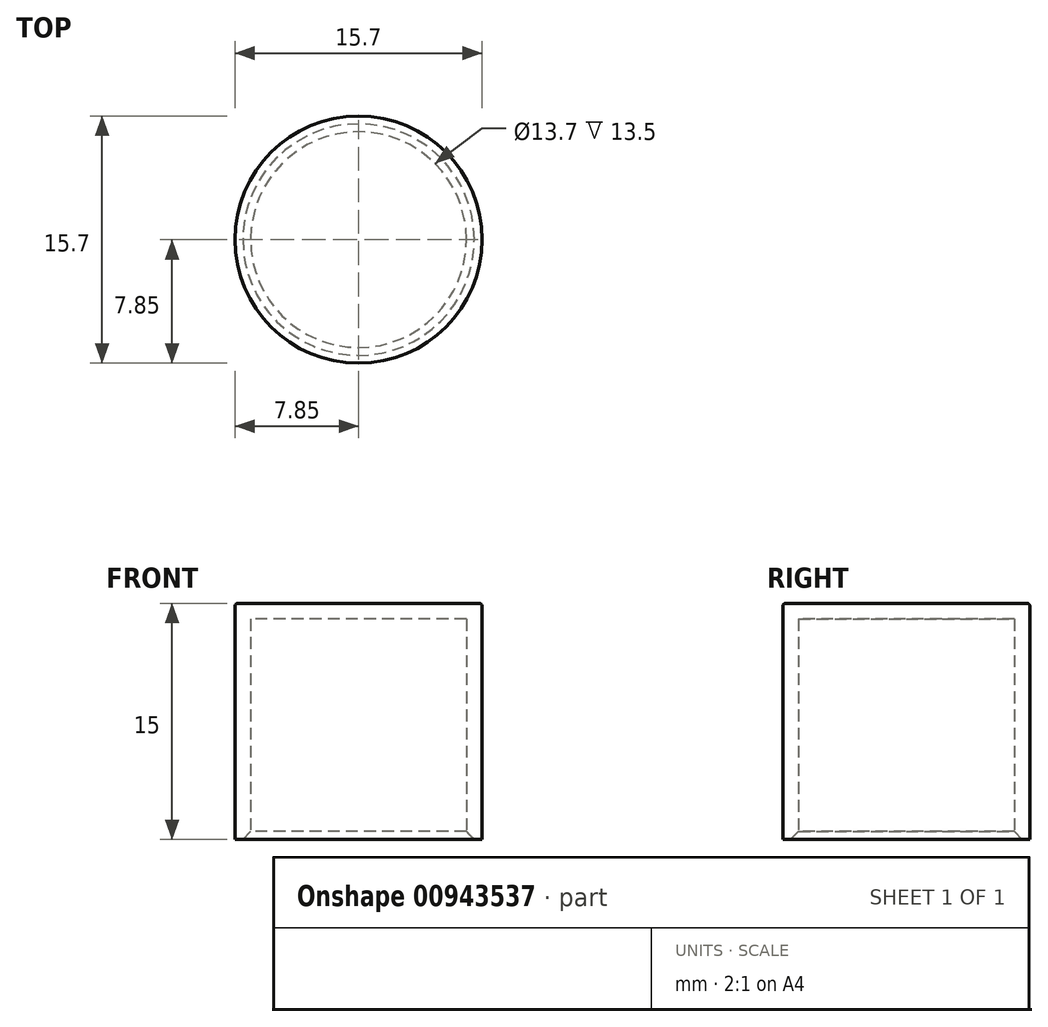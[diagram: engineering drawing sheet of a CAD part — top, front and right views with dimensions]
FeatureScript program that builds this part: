
annotation { "Feature Type Name" : "Feature", "Feature Type Description" : "" }
export const myFeature = defineFeature(function(context is Context, id is Id, definition is map)
    precondition{}
    {
        {
            var Q0;
            Q0=qCreatedBy(makeId("Top.planeOp"),FACE);
            var sketch = newSketch(context, id + "F0", { "sketchPlane" : qUnion([Q0])});
            skCircle(sketch, "E0", {"center": v(0, 0) * mm, "radius": 7.85 * mm});
            skSolve(sketch);
        }
        {
            var Q0;
            Q0=makeQuery(id+"F0.imprint","IMPRINT",FACE,{"disambiguationData":[TD([[makeQuery(id+"F0.imprint","IMPRINT",EDGE,{"derivedFrom":sQuery(id+"F0.wireOp",EDGE,"E0")}),1.0]])]});
            var Q1;
            Q1=sQuery(id+"F0.wireOp",EDGE,"E0");
            extrude(context, id + "F1", {"entities" : qUnion([Q0]), "surfaceEntities" : qUnion([Q1]), "depth" : 15 * mm, "offsetDistance" : 25.4 * mm});
        }
        {
            var Q0;
            Q0=makeQuery(id+"F1.opExtrude","CAP_FACE",FACE,{"disambiguationData":[OSD([sQuery(id+"F0.wireOp",EDGE,"E0")])],"isStart":true});
            shell(context, id + "F2", {"entities" : qUnion([Q0]), "thickness" : 1 * mm});
        }
        {
            var Q0;
            Q0=makeQuery(id+"F1.opExtrude","CAP_EDGE",EDGE,{"disambiguationData":[OSD([sQuery(id+"F0.wireOp",EDGE,"E0")])],"isStart":false});
            fillet(context, id + "F3", {"entities" : qUnion([Q0]), "radius" : 0.2 * mm, "tangentPropagation" : true, "allowEdgeOverflow" : false});
        }
        {
            var Q0;
            {var subQ0=sQuery(id+"F0.wireOp",EDGE,"E0");Q0=makeQuery(id+"F2.opShell","OFFSET_EDGE",EDGE,{"disambiguationData":[OSD([subQ0]),TDD([makeQuery(id+"F1.opExtrude","CAP_EDGE",EDGE,{"disambiguationData":[OSD([subQ0])],"isStart":true})])]});}
            chamfer(context, id + "F4", {"entities" : qUnion([Q0]), "width" : .5 * mm, "tangentPropagation" : true});
        }
    });
